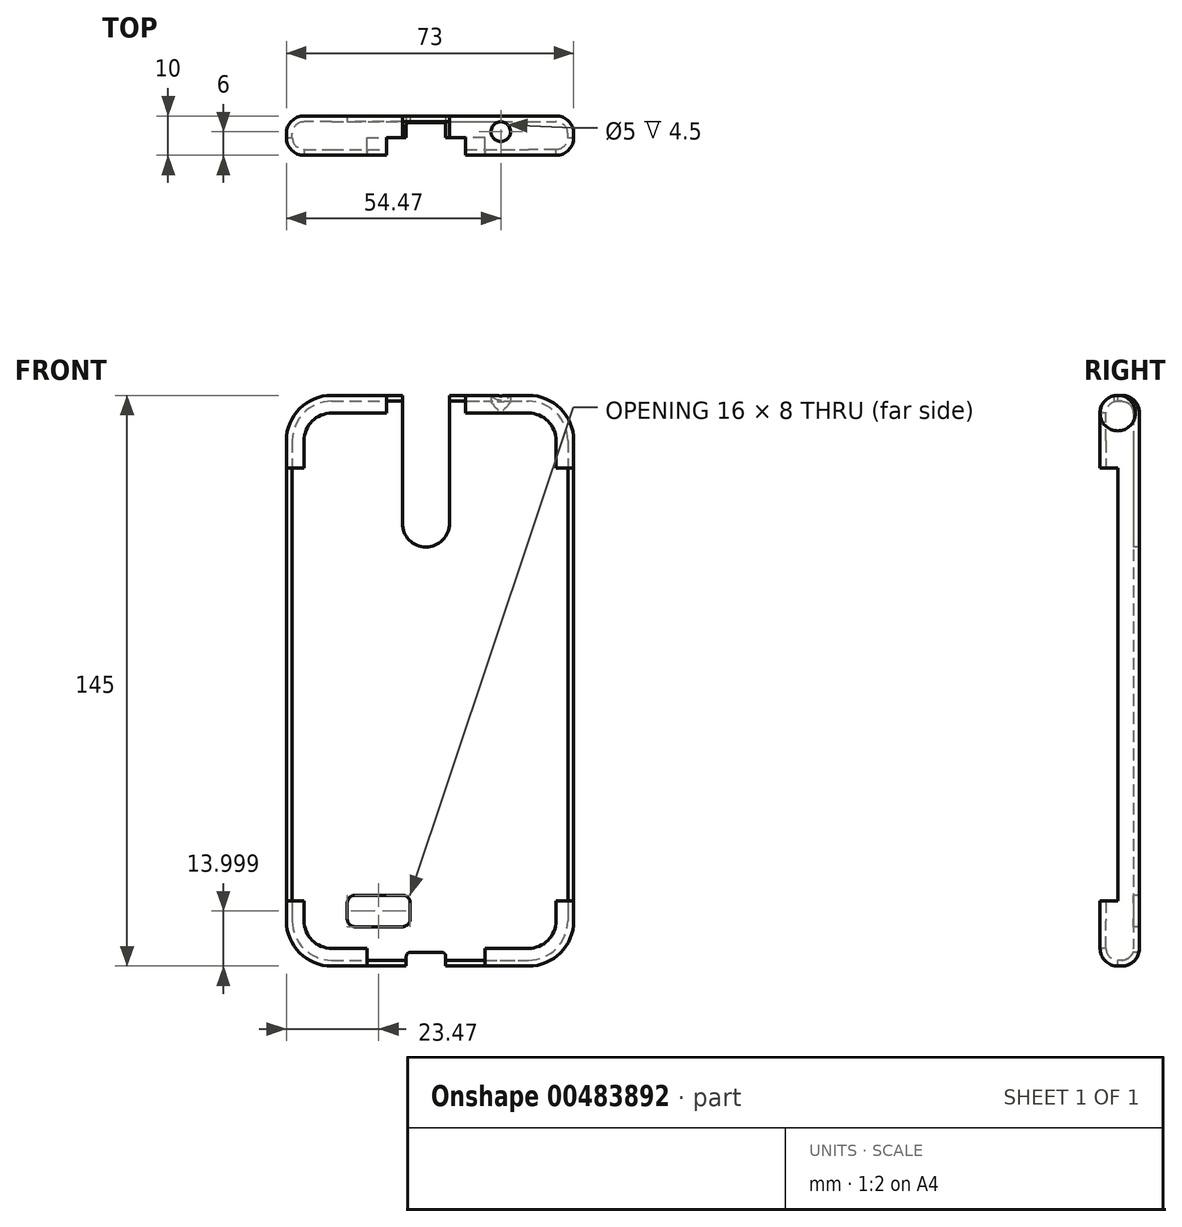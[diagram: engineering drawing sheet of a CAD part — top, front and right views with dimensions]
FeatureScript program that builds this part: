
annotation { "Feature Type Name" : "Feature", "Feature Type Description" : "" }
export const myFeature = defineFeature(function(context is Context, id is Id, definition is map)
    precondition{}
    {
        {
            var Q0;
            Q0=qCreatedBy(makeId("Front.planeOp"),FACE);
            var sketch = newSketch(context, id + "F0", { "sketchPlane" : qUnion([Q0])});
            skLineSegment(sketch, "E0.bottom", {"start": v(-33.97, 71.94) * mm, "end": v(36.03, 71.94) * mm});
            skLineSegment(sketch, "E0.top", {"start": v(-33.97, -70.06) * mm, "end": v(36.03, -70.06) * mm});
            skLineSegment(sketch, "E0.left", {"start": v(-33.97, 71.94) * mm, "end": v(-33.97, -70.06) * mm});
            skLineSegment(sketch, "E0.right", {"start": v(36.03, 71.94) * mm, "end": v(36.03, -70.06) * mm});
            skSolve(sketch);
        }
        {
            var Q0;
            Q0=makeQuery(id+"F0.imprint","IMPRINT",FACE,{"disambiguationData":[TD([[makeQuery(id+"F0.imprint","IMPRINT",EDGE,{"derivedFrom":sQuery(id+"F0.wireOp",EDGE,"E0.bottom")}),-1.0]])]});
            extrude(context, id + "F1", {"entities" : qUnion([Q0]), "depth" : 7 * mm});
        }
        {
            var Q0;
            Q0=makeQuery(id+"F1.opExtrude","SWEPT_EDGE",EDGE,{"disambiguationData":[OSD([sQuery(id+"F0.wireOp",EDGE,"E0.bottom"),sQuery(id+"F0.wireOp",EDGE,"E0.left")])]});
            var Q1;
            Q1=makeQuery(id+"F1.opExtrude","SWEPT_EDGE",EDGE,{"disambiguationData":[OSD([sQuery(id+"F0.wireOp",EDGE,"E0.bottom"),sQuery(id+"F0.wireOp",EDGE,"E0.right")])]});
            var Q2;
            Q2=makeQuery(id+"F1.opExtrude","SWEPT_EDGE",EDGE,{"disambiguationData":[OSD([sQuery(id+"F0.wireOp",EDGE,"E0.top"),sQuery(id+"F0.wireOp",EDGE,"E0.right")])]});
            var Q3;
            Q3=makeQuery(id+"F1.opExtrude","SWEPT_EDGE",EDGE,{"disambiguationData":[OSD([sQuery(id+"F0.wireOp",EDGE,"E0.top"),sQuery(id+"F0.wireOp",EDGE,"E0.left")])]});
            fillet(context, id + "F2", {"entities" : qUnion([Q0, Q1, Q2, Q3]), "radius" : 10 * mm, "tangentPropagation" : true, "allowEdgeOverflow" : false});
        }
        {
            var Q0;
            Q0=makeQuery(id+"F1.opExtrude","CAP_EDGE",EDGE,{"disambiguationData":[OSD([sQuery(id+"F0.wireOp",EDGE,"E0.left")])],"isStart":true});
            var Q1;
            Q1=makeQuery(id+"F1.opExtrude","CAP_EDGE",EDGE,{"disambiguationData":[OSD([sQuery(id+"F0.wireOp",EDGE,"E0.left")])],"isStart":false});
            fillet(context, id + "F3", {"entities" : qUnion([Q0, Q1]), "radius" : 3 * mm, "tangentPropagation" : true, "allowEdgeOverflow" : false});
        }
        {
            var Q0;
            Q0=qCreatedBy(makeId("Front.planeOp"),FACE);
            var sketch = newSketch(context, id + "F4", { "sketchPlane" : qUnion([Q0])});
            skLineSegment(sketch, "E1.bottom", {"start": v(-6, -53.56) * mm, "end": v(-18, -53.56) * mm});
            skLineSegment(sketch, "E1.top", {"start": v(-6, -61.56) * mm, "end": v(-18, -61.56) * mm});
            skLineSegment(sketch, "E1.left", {"start": v(-4, -55.56) * mm, "end": v(-4, -59.56) * mm});
            skLineSegment(sketch, "E1.right", {"start": v(-20, -55.56) * mm, "end": v(-20, -59.56) * mm});
            skArc(sketch, "E2", {"start": v(-6, 40.94) * mm, "mid": v(0, 34.94) * mm, "end": v(6, 40.94) * mm});
            skLineSegment(sketch, "E3.bottom", {"start": v(6, 80.94) * mm, "end": v(-6, 80.94) * mm});
            skLineSegment(sketch, "E3.left", {"start": v(6, 80.94) * mm, "end": v(6, 40.94) * mm});
            skLineSegment(sketch, "E3.right", {"start": v(-6, 80.94) * mm, "end": v(-6, 40.94) * mm});
            skPoint(sketch, "E4.visualSharp", {"position": v(-4, -53.56) * mm});
            skArc(sketch, "E4.filletArc", {"start": v(-4, -55.56) * mm, "mid": v(-4.59, -54.15) * mm, "end": v(-6, -53.56) * mm});
            skPoint(sketch, "E5.visualSharp", {"position": v(-20, -53.56) * mm});
            skArc(sketch, "E5.filletArc", {"start": v(-18, -53.56) * mm, "mid": v(-19.41, -54.15) * mm, "end": v(-20, -55.56) * mm});
            skPoint(sketch, "E6.visualSharp", {"position": v(-20, -61.56) * mm});
            skArc(sketch, "E6.filletArc", {"start": v(-20, -59.56) * mm, "mid": v(-19.41, -60.98) * mm, "end": v(-18, -61.56) * mm});
            skPoint(sketch, "E7.visualSharp", {"position": v(-4, -61.56) * mm});
            skArc(sketch, "E7.filletArc", {"start": v(-6, -61.56) * mm, "mid": v(-4.59, -60.98) * mm, "end": v(-4, -59.56) * mm});
            skLineSegment(sketch, "E8.bottom", {"start": v(4, -68.06) * mm, "end": v(-4, -68.06) * mm});
            skLineSegment(sketch, "E8.top", {"start": v(3, -80.06) * mm, "end": v(-3, -80.06) * mm});
            skLineSegment(sketch, "E8.left", {"start": v(5, -69.06) * mm, "end": v(5, -78.06) * mm});
            skLineSegment(sketch, "E8.right", {"start": v(-5, -69.06) * mm, "end": v(-5, -78.06) * mm});
            skPoint(sketch, "E9.visualSharp", {"position": v(5, -68.06) * mm});
            skArc(sketch, "E9.filletArc", {"start": v(5, -69.06) * mm, "mid": v(4.7, -68.35) * mm, "end": v(4, -68.06) * mm});
            skPoint(sketch, "E10.visualSharp", {"position": v(-5, -68.06) * mm});
            skArc(sketch, "E10.filletArc", {"start": v(-4, -68.06) * mm, "mid": v(-4.7, -68.35) * mm, "end": v(-5, -69.06) * mm});
            skPoint(sketch, "E11.visualSharp", {"position": v(-5, -80.06) * mm});
            skArc(sketch, "E11.filletArc", {"start": v(-5, -78.06) * mm, "mid": v(-4.41, -79.48) * mm, "end": v(-3, -80.06) * mm});
            skPoint(sketch, "E12.visualSharp", {"position": v(5, -80.06) * mm});
            skArc(sketch, "E12.filletArc", {"start": v(3, -80.06) * mm, "mid": v(4.41, -79.48) * mm, "end": v(5, -78.06) * mm});
            skSolve(sketch);
        }
        {
            var Q0;
            Q0=makeQuery(id+"F1.opExtrude","CAP_FACE",FACE,{"disambiguationData":[OSD([sQuery(id+"F0.wireOp",EDGE,"E0.bottom"),sQuery(id+"F0.wireOp",EDGE,"E0.top"),sQuery(id+"F0.wireOp",EDGE,"E0.left"),sQuery(id+"F0.wireOp",EDGE,"E0.right")])],"isStart":false});
            shell(context, id + "F5", {"entities" : qUnion([Q0]), "thickness" : 1.5 * mm, "oppositeDirection" : true});
        }
        {
            var Q0;
            Q0 = qSketchRegion(id + "F4", true);
            extrude(context, id + "F6", {"entities" : qUnion([Q0]), "operationType" : NewBodyOperationType.REMOVE, "oppositeDirection" : true, "depth" : 10 * mm, "hasSecondDirection" : true, "secondDirectionOppositeDirection" : false, "secondDirectionDepth" : 10 * mm});
        }
        {
            var Q0;
            Q0=qCreatedBy(makeId("Top.planeOp"),FACE);
            var sketch = newSketch(context, id + "F7", { "sketchPlane" : qUnion([Q0])});
            skCircle(sketch, "E13", {"center": v(19, -2.5) * mm, "radius": 2.5 * mm});
            skSolve(sketch);
        }
        {
            var Q0;
            Q0 = qSketchRegion(id + "F7", true);
            extrude(context, id + "F8", {"entities" : qUnion([Q0]), "operationType" : NewBodyOperationType.REMOVE, "depth" : 90 * mm});
        }
        {
            var Q0;
            Q0=qCreatedBy(makeId("Front.planeOp"),FACE);
            var sketch = newSketch(context, id + "F9", { "sketchPlane" : qUnion([Q0])});
            skLineSegment(sketch, "E14.right", {"start": v(50, 55) * mm, "end": v(50, -55) * mm});
            skLineSegment(sketch, "E15.right", {"start": v(10, 80) * mm, "end": v(10, 55) * mm});
            skLineSegment(sketch, "E16.trimOffspring", {"start": v(10, 55) * mm, "end": v(50, 55) * mm});
            skLineSegment(sketch, "E17.trimOffspring", {"start": v(15, -55) * mm, "end": v(15, -80) * mm});
            skLineSegment(sketch, "E18.trimOffspring", {"start": v(15, -55) * mm, "end": v(50, -55) * mm});
            skLineSegment(sketch, "E19", {"start": v(-10, 55) * mm, "end": v(-50, 55) * mm});
            skLineSegment(sketch, "E20", {"start": v(-50, 55) * mm, "end": v(-50, -55) * mm});
            skLineSegment(sketch, "E21", {"start": v(-50, -55) * mm, "end": v(-15, -55) * mm});
            skLineSegment(sketch, "E22", {"start": v(-15, -55) * mm, "end": v(-15, -80) * mm});
            skLineSegment(sketch, "E23", {"start": v(-10, 80) * mm, "end": v(-10, 55) * mm});
            skLineSegment(sketch, "E24", {"start": v(-10, 80) * mm, "end": v(10, 80) * mm});
            skLineSegment(sketch, "E25", {"start": v(-15, -80) * mm, "end": v(15, -80) * mm});
            skSolve(sketch);
        }
        {
            var Q0;
            Q0 = qSketchRegion(id + "F9", true);
            extrude(context, id + "F10", {"entities" : qUnion([Q0]), "operationType" : NewBodyOperationType.REMOVE, "depth" : 25 * mm, "hasSecondDirection" : true, "secondDirectionOppositeDirection" : false, "secondDirectionDepth" : 4 * mm});
        }
    });
